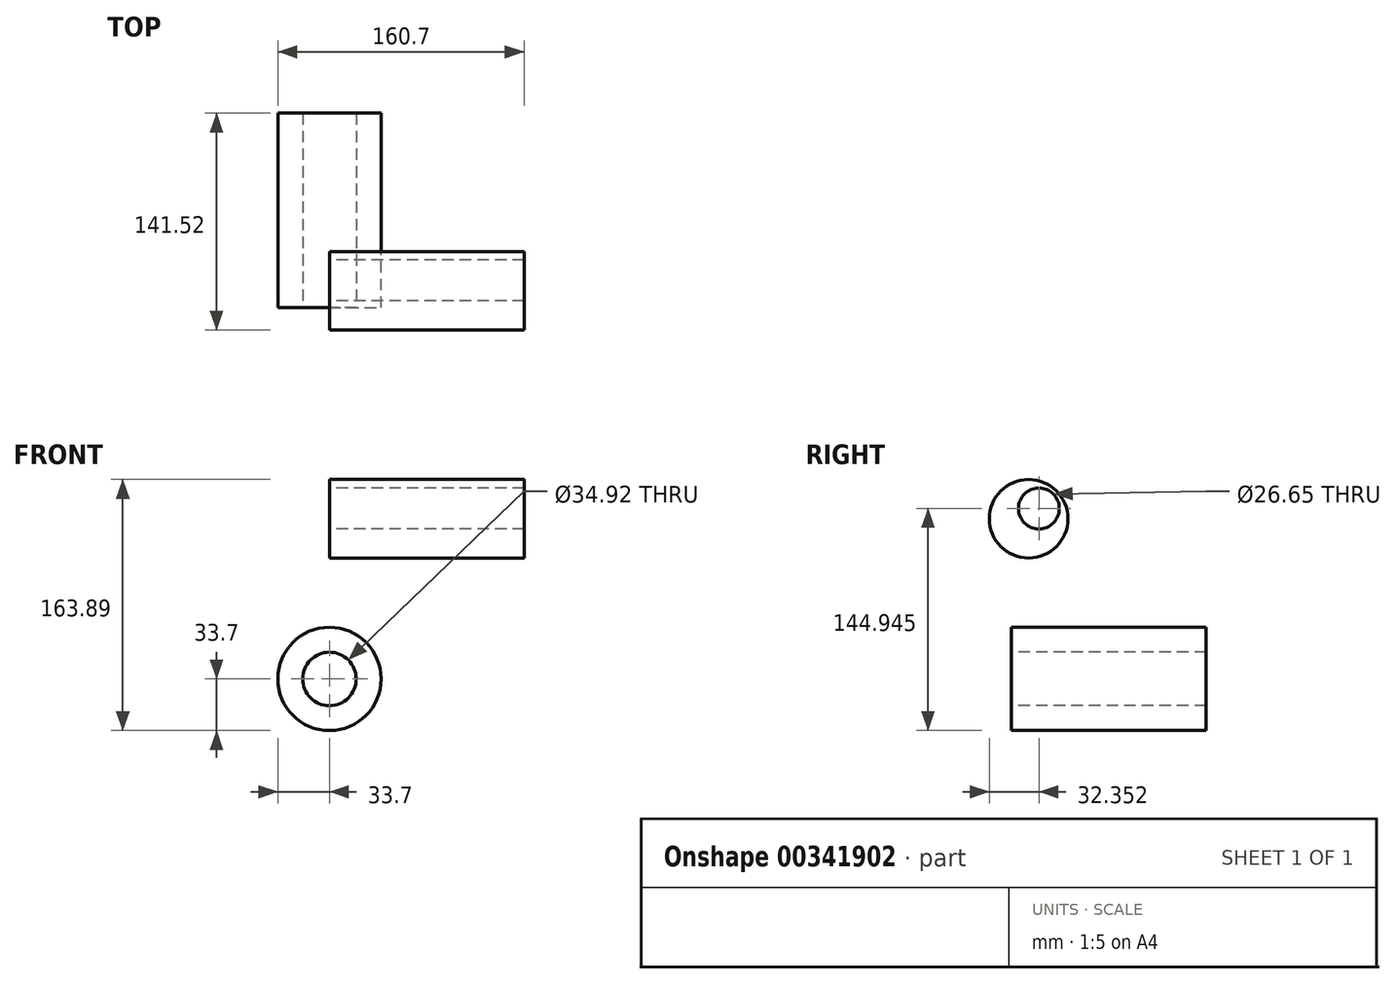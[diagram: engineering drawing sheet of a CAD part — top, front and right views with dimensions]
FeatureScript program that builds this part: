
annotation { "Feature Type Name" : "Feature", "Feature Type Description" : "" }
export const myFeature = defineFeature(function(context is Context, id is Id, definition is map)
    precondition{}
    {
        {
            var Q0;
            Q0=qCreatedBy(makeId("Front.planeOp"),FACE);
            var sketch = newSketch(context, id + "F0", { "sketchPlane" : qUnion([Q0])});
            skCircle(sketch, "E0", {"center": v(0, 0) * mm, "radius": 33.7 * mm});
            skSolve(sketch);
        }
        {
            var Q0;
            Q0=makeQuery(id+"F0.imprint","IMPRINT",FACE,{"disambiguationData":[TD([[makeQuery(id+"F0.imprint","IMPRINT",EDGE,{"derivedFrom":sQuery(id+"F0.wireOp",EDGE,"E0")}),1.0]])]});
            extrude(context, id + "F1", {"entities" : qUnion([Q0]), "depth" : 127 * mm});
        }
        {
            var Q0;
            Q0=makeQuery(id+"F1.opExtrude","CAP_FACE",FACE,{"disambiguationData":[OSD([sQuery(id+"F0.wireOp",EDGE,"E0")])],"isStart":false});
            var sketch = newSketch(context, id + "F2", { "sketchPlane" : qUnion([Q0])});
            skCircle(sketch, "E1", {"center": v(0, 0) * mm, "radius": 17.46 * mm});
            skSolve(sketch);
        }
        {
            var Q0;
            Q0 = qSketchRegion(id + "F2", true);
            extrude(context, id + "F3", {"entities" : qUnion([Q0]), "operationType" : NewBodyOperationType.REMOVE, "oppositeDirection" : true, "depth" : 146.3 * mm});
        }
        {
            var Q0;
            Q0=qCreatedBy(makeId("Right.planeOp"),FACE);
            var sketch = newSketch(context, id + "F4", { "sketchPlane" : qUnion([Q0])});
            skCircle(sketch, "E2", {"center": v(-115.87, 104.54) * mm, "radius": 25.65 * mm});
            skSolve(sketch);
        }
        {
            var Q0;
            Q0=makeQuery(id+"F4.imprint","IMPRINT",FACE,{"disambiguationData":[TD([[makeQuery(id+"F4.imprint","IMPRINT",EDGE,{"derivedFrom":sQuery(id+"F4.wireOp",EDGE,"E2")}),1.0]])]});
            extrude(context, id + "F5", {"entities" : qUnion([Q0]), "depth" : 127 * mm});
        }
        {
            var Q0;
            Q0=makeQuery(id+"F5.opExtrude","CAP_FACE",FACE,{"disambiguationData":[OSD([sQuery(id+"F4.wireOp",EDGE,"E2")])],"isStart":true});
            var sketch = newSketch(context, id + "F6", { "sketchPlane" : qUnion([Q0])});
            skCircle(sketch, "E3", {"center": v(109.17, 111.24) * mm, "radius": 13.32 * mm});
            skSolve(sketch);
        }
        {
            var Q0;
            Q0=makeQuery(id+"F6.imprint","IMPRINT",FACE,{"disambiguationData":[TD([[makeQuery(id+"F6.imprint","IMPRINT",EDGE,{"derivedFrom":sQuery(id+"F6.wireOp",EDGE,"E3")}),1.0]])]});
            var Q1;
            Q1=sQuery(id+"F6.wireOp",EDGE,"E3");
            extrude(context, id + "F7", {"entities" : qUnion([Q0]), "operationType" : NewBodyOperationType.REMOVE, "surfaceEntities" : qUnion([Q1]), "oppositeDirection" : true, "depth" : 127 * mm});
        }
    });
